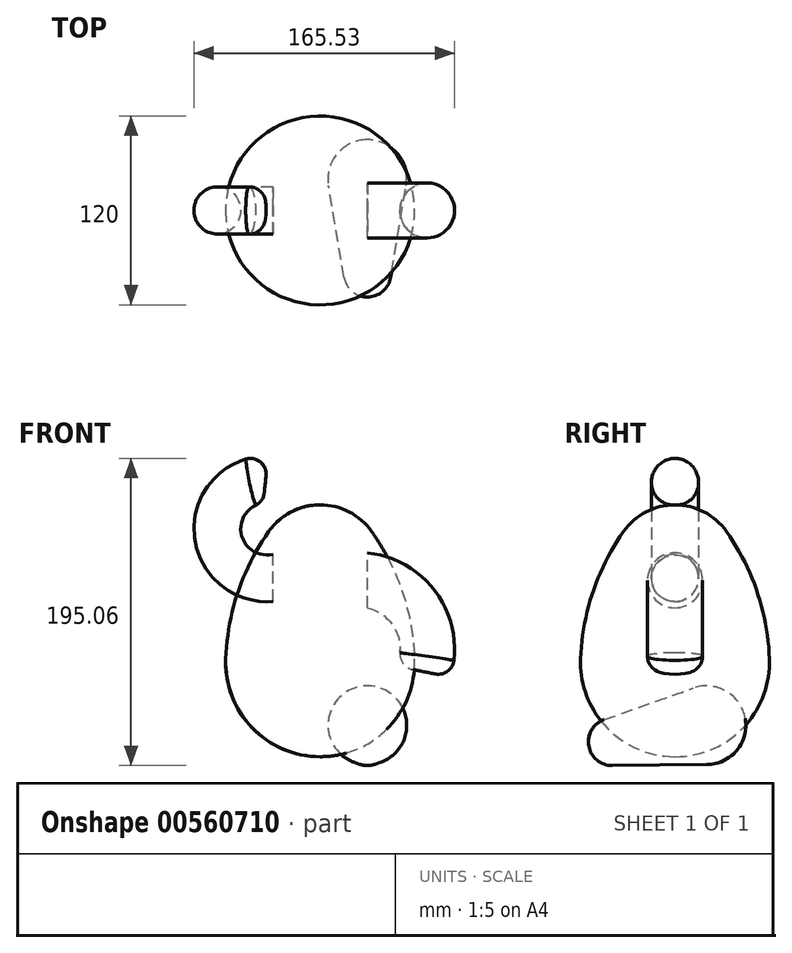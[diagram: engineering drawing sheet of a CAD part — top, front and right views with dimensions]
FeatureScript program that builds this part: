
annotation { "Feature Type Name" : "Feature", "Feature Type Description" : "" }
export const myFeature = defineFeature(function(context is Context, id is Id, definition is map)
    precondition{}
    {
        {
            var Q0;
            Q0=qCreatedBy(makeId("Front.planeOp"),FACE);
            var sketch = newSketch(context, id + "F0", { "sketchPlane" : qUnion([Q0])});
            skArc(sketch, "E0", {"start": v(-59.96, 2.22) * mm, "mid": v(-43.2, -41.63) * mm, "end": v(0, -60) * mm});
            skArc(sketch, "E1", {"start": v(0, 100) * mm, "mid": v(-18.42, 95.5) * mm, "end": v(-32.7, 83.03) * mm});
            skArc(sketch, "E2", {"start": v(-32.7, 83.03) * mm, "mid": v(-52.2, 44.6) * mm, "end": v(-59.96, 2.22) * mm});
            skLineSegment(sketch, "E3", {"start": v(0, 100) * mm, "end": v(0, -70.65) * mm, "construction": true});
            skPoint(sketch, "E3.endSnap0", {"position": v(0, 100) * mm});
            skLineSegment(sketch, "E4", {"start": v(0, 100) * mm, "end": v(0, -60) * mm});
            skSolve(sketch);
        }
        {
            var Q0;
            Q0=makeQuery(id+"F0.imprint","IMPRINT",FACE,{"disambiguationData":[TD([[makeQuery(id+"F0.imprint","IMPRINT",EDGE,{"derivedFrom":sQuery(id+"F0.wireOp",EDGE,"E0")}),1.0]])]});
            var Q1;
            Q1=sQuery(id+"F0.wireOp",EDGE,"E4");
            revolve(context, id + "F1", {"entities" : qUnion([Q0]), "axis" : qUnion([Q1]), "revolveType" : RevolveType.FULL});
        }
        {
            var Q0;
            Q0=qCreatedBy(makeId("Right.planeOp"),FACE);
            cPlane(context, id + "F2", {"entities" : qUnion([Q0]), "cplaneType" : CPlaneType.OFFSET, "offset" : 30 * mm, "width" : 150 * mm, "height" : 150 * mm});
        }
        {
            var Q0;
            Q0=qCreatedBy(id+"F2.planeOp",FACE);
            var sketch = newSketch(context, id + "F3", { "sketchPlane" : qUnion([Q0])});
            skLineSegment(sketch, "E5", {"start": v(20, -40) * mm, "end": v(-40, -50.58) * mm, "construction": true});
            skArc(sketch, "E6", {"start": v(-54.77, -53.18) * mm, "mid": v(-49.59, -62.12) * mm, "end": v(-39.86, -65.58) * mm});
            skArc(sketch, "E7", {"start": v(20.24, -65) * mm, "mid": v(39.23, -55.98) * mm, "end": v(44.62, -35.66) * mm});
            skLineSegment(sketch, "E8", {"start": v(-39.86, -65.58) * mm, "end": v(20.24, -65) * mm});
            skLineSegment(sketch, "E9", {"start": v(-54.77, -53.18) * mm, "end": v(44.62, -35.66) * mm});
            skSolve(sketch);
        }
        {
            var Q0;
            Q0=makeQuery(id+"F3.imprint","IMPRINT",FACE,{"disambiguationData":[TD([[makeQuery(id+"F3.imprint","IMPRINT",EDGE,{"derivedFrom":sQuery(id+"F3.wireOp",EDGE,"E6")}),1.0]])]});
            var Q1;
            Q1=sQuery(id+"F3.wireOp",EDGE,"E5");
            revolve(context, id + "F4", {"entities" : qUnion([Q0]), "axis" : qUnion([Q1]), "revolveType" : RevolveType.FULL});
        }
        {
            var Q0;
            Q0=qCreatedBy(makeId("Front.planeOp"),FACE);
            var sketch = newSketch(context, id + "F5", { "sketchPlane" : qUnion([Q0])});
            skArc(sketch, "E10", {"start": v(81.45, -11.15) * mm, "mid": v(75.52, 40.3) * mm, "end": v(32.1, 68.5) * mm});
            skSolve(sketch);
        }
        {
            var Q0;
            Q0=qCreatedBy(id+"F2.planeOp",FACE);
            var sketch = newSketch(context, id + "F6", { "sketchPlane" : qUnion([Q0])});
            skCircle(sketch, "E11", {"center": v(0, 52.04) * mm, "radius": 17.47 * mm});
            skSolve(sketch);
        }
        {
            var Q0;
            Q0=makeQuery(id+"F6.imprint","IMPRINT",FACE,{"disambiguationData":[TD([[makeQuery(id+"F6.imprint","IMPRINT",EDGE,{"derivedFrom":sQuery(id+"F6.wireOp",EDGE,"E11")}),1.0]])]});
            var Q1;
            Q1=sQuery(id+"F5.wireOp",EDGE,"E10");
            sweep(context, id + "F7", {"profiles" : qUnion([Q0]), "path" : qUnion([Q1])});
        }
        {
            var Q0;
            Q0=makeQuery(id+"F7.opSweep","CAP_FACE",FACE,{"disambiguationData":[OSD([sQuery(id+"F5.wireOp",VERTEX,"E10.start"),sQuery(id+"F6.wireOp",EDGE,"E11")])],"isStart":false});
            fillet(context, id + "F8", {"entities" : qUnion([Q0]), "radius" : 10 * mm, "tangentPropagation" : true, "allowEdgeOverflow" : false});
        }
        {
            var Q0;
            Q0=qCreatedBy(makeId("Front.planeOp"),FACE);
            var sketch = newSketch(context, id + "F9", { "sketchPlane" : qUnion([Q0])});
            skArc(sketch, "E12", {"start": v(-34.79, 114.74) * mm, "mid": v(-63.77, 82.35) * mm, "end": v(-30, 55) * mm});
            skSolve(sketch);
        }
        {
            var Q0;
            Q0=qCreatedBy(makeId("Right.planeOp"),FACE);
            cPlane(context, id + "F10", {"entities" : qUnion([Q0]), "cplaneType" : CPlaneType.OFFSET, "offset" : 30 * mm, "oppositeDirection" : true, "width" : 150 * mm, "height" : 150 * mm});
        }
        {
            var Q0;
            Q0=qCreatedBy(id+"F10.planeOp",FACE);
            var sketch = newSketch(context, id + "F11", { "sketchPlane" : qUnion([Q0])});
            skCircle(sketch, "E13", {"center": v(0, 53.63) * mm, "radius": 15 * mm});
            skSolve(sketch);
        }
        {
            var Q0;
            Q0=makeQuery(id+"F11.imprint","IMPRINT",FACE,{"disambiguationData":[TD([[makeQuery(id+"F11.imprint","IMPRINT",EDGE,{"derivedFrom":sQuery(id+"F11.wireOp",EDGE,"E13")}),1.0]])]});
            var Q1;
            Q1=sQuery(id+"F9.wireOp",EDGE,"E12");
            sweep(context, id + "F12", {"profiles" : qUnion([Q0]), "path" : qUnion([Q1])});
        }
        {
            var Q0;
            Q0=makeQuery(id+"F12.opSweep","CAP_EDGE",EDGE,{"disambiguationData":[OSD([sQuery(id+"F9.wireOp",VERTEX,"E12.start"),sQuery(id+"F11.wireOp",EDGE,"E13")])],"isStart":false});
            fillet(context, id + "F13", {"entities" : qUnion([Q0]), "radius" : 10 * mm, "tangentPropagation" : true, "allowEdgeOverflow" : false});
        }
        {
            var Q0;
            Q0=qCreatedBy(id+"F2.planeOp",FACE);
            var sketch = newSketch(context, id + "F14", { "sketchPlane" : qUnion([Q0])});
            skLineSegment(sketch, "E14", {"start": v(0, 63.36) * mm, "end": v(0, -108.21) * mm});
            skSolve(sketch);
        }
    });
